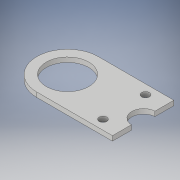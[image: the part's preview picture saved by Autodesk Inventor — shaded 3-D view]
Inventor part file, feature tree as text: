
AUTODESK INVENTOR PART (.ipt)
format: ipt  version: 2018 (Build 220112000, 112)  size: 116,224 bytes
history: native  units: in
note: dims shown in document units (in); Inventor stores cm internally (conversion verified against a paired STEP export)
features: extrude x1, sketch x1
ambient origin geometry x8: Origin, YZ Plane, XZ Plane, XY Plane, X Axis, Y Axis, Z Axis, Center Point
bodies: Solid1 (feature_tree)
feature tree (2):
  extrude  "Extrusion1"  Depth=0.125in
  sketch  "Sketch1"  dims[d0=1.125in d1=0.25in d2=2.0in d3=2.0in d4=0.5in d5=0.5in d6=0.5in d7=0.2031in d8=0.2031in d9=0.125in d10=0.0in]
